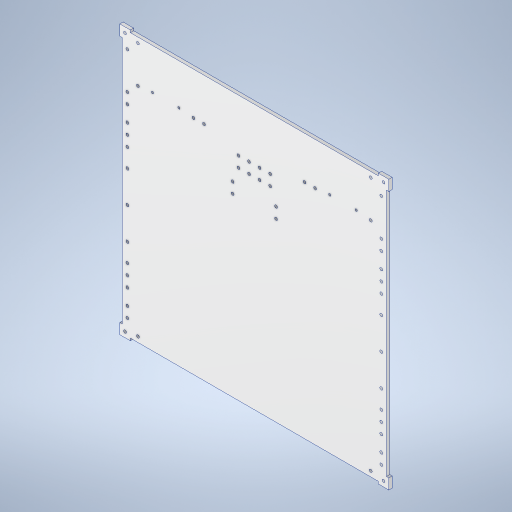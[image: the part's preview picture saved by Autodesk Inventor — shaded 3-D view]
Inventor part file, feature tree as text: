
AUTODESK INVENTOR PART (.ipt)
format: ipt  version: 2024 (Build 280153000, 153)  size: 536,576 bytes
history: native  units: mm
features: sketch x8, hole x7, projected_geometry x5, extrude x2, mirror x1
ambient origin geometry x8: Origin, YZ Plane, XZ Plane, XY Plane, X Axis, Y Axis, Z Axis, Center Point
bodies: Solid1 (feature_tree)
feature tree (23):
  sketch  "Sketch1"  dims[d0=508.7mm d1=508.7mm]
  extrude  "Extrusion1"  Depth=508.7mm
  hole  "Hole1"  [1 undecoded]
  hole  "Hole2"  [1 undecoded]
  hole  "Hole3"  [1 undecoded]
  hole  "Hole4"  [1 undecoded]
  hole  "Hole5"  [1 undecoded]
  mirror  "Mirror1"
  hole  "Hole6"  [1 undecoded]
  hole  "Hole7"  [1 undecoded]
  extrude  "Extrusion2"  Depth=4.35mm
  sketch  "Sketch3"  dims[d2=20.0mm d3=20.0mm]
  sketch  "Sketch4"  dims[d4=40.0mm d5=40.0mm]
  projected_geometry  "Projected Loop1"
  sketch  "Sketch5"  dims[d6=4.35mm d7=4.35mm]
  projected_geometry  "Projected Loop2"
  sketch  "Sketch6"  dims[d8=20.0mm d9=20.0mm]
  sketch  "Sketch7"  dims[d10=4.35mm d11=4.35mm]
  projected_geometry  "Projected Loop3"
  sketch  "Sketch8"  dims[d12=4.35mm d13=4.35mm]
  projected_geometry  "Projected Loop4"
  sketch  "Sketch9"  dims[d14=4.35mm d15=4.35mm d16=4.35mm d17=70.0mm d18=80.0mm d19=40.0mm d20=60.0mm d21=20.0mm d22=20.0mm d23=20.0mm d24=40.0mm d25=20.0mm d28=20.0mm d30=20.0mm d33=50.0mm d34=6.35mm d35=0.0mm d36=5.3mm d37=6.0mm d38=4.0mm d39=2.0mm d40=90.0deg d41=8.0mm d42=20.594885mm d43=82.0mm d44=20.0mm d45=54.0mm d46=54.0mm d47=1.0mm d48=28.0mm d49=5.3mm d50=6.0mm d51=4.0mm d52=2.0mm d53=90.0deg d54=15.0mm d55=0.0mm d59=50.0mm d60=30.0mm d63=235.0mm d65=470.0mm d66=43.5mm d67=43.5mm d68=4.134mm d69=10.0mm d70=4.0mm d71=2.0mm d72=90.0deg d73=8.0mm d74=20.594885mm d75=50.0mm d76=3.0mm d77=4.134mm d78=10.0mm d79=4.0mm d80=2.0mm d81=90.0deg d82=8.0mm d83=20.594885mm d84=1.0mm d85=12.0mm d86=130.0mm d87=102.0mm d88=232.0mm d89=20.0mm d90=4.134mm d91=10.0mm d92=4.0mm d93=2.0mm d94=90.0deg d95=8.0mm d96=20.594885mm d100=50.0mm d101=50.0mm d102=170.0mm d103=45.0mm d104=45.0mm d105=170.0mm d106=30.0mm d107=30.0mm d108=30.0mm d109=30.0mm d110=5.4mm d111=6.0mm d112=4.0mm d113=2.0mm d114=90.0deg d115=8.0mm d116=20.594885mm d117=120.0mm d118=120.0mm d119=5.4mm d120=6.0mm d121=4.0mm d122=2.0mm d123=90.0deg d124=8.0mm d125=20.594885mm d132=20.0mm d135=10.0mm d136=10.0mm d137=0.0mm d138=0.0mm d139=219.35mm d140=156.0mm]
  projected_geometry  "Projected Loop5"
note: 7 required parameter values undecoded (feature->parameter linkage not recoverable at this tier; creation-order binding heuristic only, values carry confidence <= 0.55)
